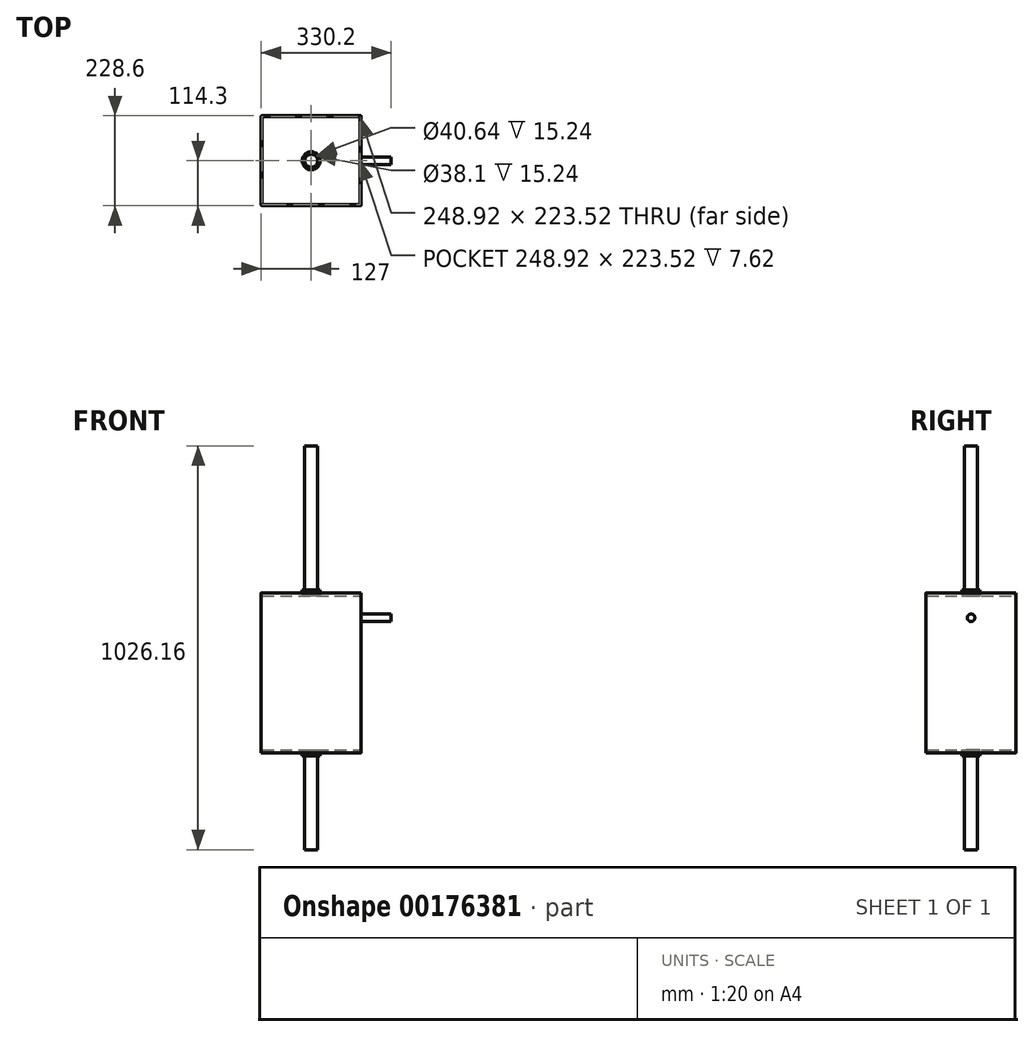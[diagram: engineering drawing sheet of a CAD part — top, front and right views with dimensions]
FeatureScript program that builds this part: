
annotation { "Feature Type Name" : "Feature", "Feature Type Description" : "" }
export const myFeature = defineFeature(function(context is Context, id is Id, definition is map)
    precondition{}
    {
        {
            var Q0;
            Q0=qCreatedBy(makeId("Front.planeOp"),FACE);
            var sketch = newSketch(context, id + "F0", { "sketchPlane" : qUnion([Q0])});
            skLineSegment(sketch, "E0.bottom", {"start": v(0, 406.4) * mm, "end": v(254, 406.4) * mm});
            skLineSegment(sketch, "E0.top", {"start": v(0, 0) * mm, "end": v(254, 0) * mm});
            skLineSegment(sketch, "E0.left", {"start": v(0, 406.4) * mm, "end": v(0, 0) * mm});
            skLineSegment(sketch, "E0.right", {"start": v(254, 406.4) * mm, "end": v(254, 0) * mm});
            skSolve(sketch);
        }
        {
            var Q0;
            Q0 = qSketchRegion(id + "F0", true);
            extrude(context, id + "F1", {"entities" : qUnion([Q0]), "depth" : 228.6 * mm});
        }
        {
            var Q0;
            Q0=makeQuery(id+"F1.opExtrude","SWEPT_FACE",FACE,{"disambiguationData":[OSD([sQuery(id+"F0.wireOp",EDGE,"E0.bottom")])]});
            var sketch = newSketch(context, id + "F2", { "sketchPlane" : qUnion([Q0])});
            skLineSegment(sketch, "E1.bottom", {"start": v(2.54, -226.06) * mm, "end": v(251.46, -226.06) * mm});
            skLineSegment(sketch, "E1.top", {"start": v(2.54, -2.54) * mm, "end": v(251.46, -2.54) * mm});
            skLineSegment(sketch, "E1.left", {"start": v(2.54, -226.06) * mm, "end": v(2.54, -2.54) * mm});
            skLineSegment(sketch, "E1.right", {"start": v(251.46, -226.06) * mm, "end": v(251.46, -2.54) * mm});
            skSolve(sketch);
        }
        {
            var Q0;
            Q0 = qSketchRegion(id + "F2", true);
            extrude(context, id + "F3", {"entities" : qUnion([Q0]), "operationType" : NewBodyOperationType.REMOVE, "oppositeDirection" : true, "depth" : 7.62 * mm});
        }
        {
            var Q0;
            Q0=makeQuery(id+"F1.opExtrude","SWEPT_FACE",FACE,{"disambiguationData":[OSD([sQuery(id+"F0.wireOp",EDGE,"E0.top")])]});
            var sketch = newSketch(context, id + "F4", { "sketchPlane" : qUnion([Q0])});
            skLineSegment(sketch, "E2.bottom", {"start": v(2.54, 226.06) * mm, "end": v(251.46, 226.06) * mm});
            skLineSegment(sketch, "E2.top", {"start": v(2.54, 2.54) * mm, "end": v(251.46, 2.54) * mm});
            skLineSegment(sketch, "E2.left", {"start": v(2.54, 226.06) * mm, "end": v(2.54, 2.54) * mm});
            skLineSegment(sketch, "E2.right", {"start": v(251.46, 226.06) * mm, "end": v(251.46, 2.54) * mm});
            skSolve(sketch);
        }
        {
            var Q0;
            Q0 = qSketchRegion(id + "F4", true);
            extrude(context, id + "F5", {"entities" : qUnion([Q0]), "operationType" : NewBodyOperationType.REMOVE, "oppositeDirection" : true, "depth" : 7.62 * mm});
        }
        {
            var Q0;
            Q0=makeQuery(id+"F5.boolean.opBoolean","COPY",FACE,{"derivedFrom":makeQuery(id+"F5.opExtrude","CAP_FACE",FACE,{"disambiguationData":[OSD([sQuery(id+"F4.wireOp",EDGE,"E2.bottom"),sQuery(id+"F4.wireOp",EDGE,"E2.top"),sQuery(id+"F4.wireOp",EDGE,"E2.left"),sQuery(id+"F4.wireOp",EDGE,"E2.right")])],"isStart":false})});
            var sketch = newSketch(context, id + "F6", { "sketchPlane" : qUnion([Q0])});
            skCircle(sketch, "E3", {"center": v(127, 114.3) * mm, "radius": 22.86 * mm});
            skCircle(sketch, "E4", {"center": v(127, 114.3) * mm, "radius": 20.32 * mm});
            skSolve(sketch);
        }
        {
            var Q0;
            Q0 = qSketchRegion(id + "F6", true);
            extrude(context, id + "F7", {"entities" : qUnion([Q0]), "depth" : 15.24 * mm});
        }
        {
            var Q0;
            Q0=makeQuery(id+"F5.boolean.opBoolean","COPY",FACE,{"derivedFrom":makeQuery(id+"F5.opExtrude","CAP_FACE",FACE,{"disambiguationData":[OSD([sQuery(id+"F4.wireOp",EDGE,"E2.bottom"),sQuery(id+"F4.wireOp",EDGE,"E2.top"),sQuery(id+"F4.wireOp",EDGE,"E2.left"),sQuery(id+"F4.wireOp",EDGE,"E2.right")])],"isStart":false})});
            var sketch = newSketch(context, id + "F8", { "sketchPlane" : qUnion([Q0])});
            skCircle(sketch, "E5", {"center": v(127, 114.3) * mm, "radius": 16.51 * mm});
            skSolve(sketch);
        }
        {
            var Q0;
            Q0 = qSketchRegion(id + "F8", true);
            var Q1;
            Q1 = qConstructionFilter(qBodyType(qCreatedBy(id + "F8" ,EDGE), BodyType.WIRE), ConstructionObject.NO);
            extrude(context, id + "F9", {"entities" : qUnion([Q0]), "surfaceEntities" : qUnion([Q1]), "depth" : 254 * mm});
        }
        {
            var Q0;
            Q0=makeQuery(id+"F1.opExtrude","CAP_EDGE",EDGE,{"disambiguationData":[OSD([sQuery(id+"F0.wireOp",EDGE,"E0.left")])],"isStart":false});
            var Q1;
            Q1=makeQuery(id+"F1.opExtrude","CAP_EDGE",EDGE,{"disambiguationData":[OSD([sQuery(id+"F0.wireOp",EDGE,"E0.left")])],"isStart":true});
            var Q2;
            {var subQ0=sQuery(id+"F0.wireOp",EDGE,"E0.bottom");var subQ1=sQuery(id+"F0.wireOp",EDGE,"E0.right");Q2=makeQuery(id+"FteSAe2NLqNJWqs_1.boolean.opBoolean","SPLIT",EDGE,{"disambiguationData":[TD([makeQuery(id+"F1.opExtrude","SWEPT_FACE",FACE,{"disambiguationData":[OSD([subQ0])]})])],"derivedFrom":makeQuery(id+"F1.opExtrude","CAP_EDGE",EDGE,{"disambiguationData":[OSD([subQ1])],"isStart":false})});}
            var Q3;
            {var subQ0=sQuery(id+"F0.wireOp",EDGE,"E0.bottom");var subQ1=sQuery(id+"F0.wireOp",EDGE,"E0.right");Q3=makeQuery(id+"FteSAe2NLqNJWqs_1.boolean.opBoolean","SPLIT",EDGE,{"disambiguationData":[TD([makeQuery(id+"F1.opExtrude","SWEPT_FACE",FACE,{"disambiguationData":[OSD([subQ0])]})])],"derivedFrom":makeQuery(id+"F1.opExtrude","CAP_EDGE",EDGE,{"disambiguationData":[OSD([subQ1])],"isStart":true})});}
            var Q4;
            {var subQ0=sQuery(id+"F0.wireOp",EDGE,"E0.right");var subQ1=sQuery(id+"F0.wireOp",EDGE,"E0.top");Q4=makeQuery(id+"FteSAe2NLqNJWqs_1.boolean.opBoolean","SPLIT",EDGE,{"disambiguationData":[TD([makeQuery(id+"F1.opExtrude","SWEPT_FACE",FACE,{"disambiguationData":[OSD([subQ1])]})])],"derivedFrom":makeQuery(id+"F1.opExtrude","CAP_EDGE",EDGE,{"disambiguationData":[OSD([subQ0])],"isStart":false})});}
            var Q5;
            {var subQ0=sQuery(id+"F0.wireOp",EDGE,"E0.right");var subQ1=sQuery(id+"F0.wireOp",EDGE,"E0.top");Q5=makeQuery(id+"FteSAe2NLqNJWqs_1.boolean.opBoolean","SPLIT",EDGE,{"disambiguationData":[TD([makeQuery(id+"F1.opExtrude","SWEPT_FACE",FACE,{"disambiguationData":[OSD([subQ1])]})])],"derivedFrom":makeQuery(id+"F1.opExtrude","CAP_EDGE",EDGE,{"disambiguationData":[OSD([subQ0])],"isStart":true})});}
            fillet(context, id + "F10", {"entities" : qUnion([Q0, Q1, Q2, Q3, Q4, Q5]), "radius" : 1.78 * mm, "tangentPropagation" : true, "allowEdgeOverflow" : false});
        }
        {
            var Q0;
            Q0=makeQuery(id+"F3.boolean.opBoolean","COPY",FACE,{"derivedFrom":makeQuery(id+"F3.opExtrude","CAP_FACE",FACE,{"disambiguationData":[OSD([sQuery(id+"F2.wireOp",EDGE,"E1.bottom"),sQuery(id+"F2.wireOp",EDGE,"E1.top"),sQuery(id+"F2.wireOp",EDGE,"E1.left"),sQuery(id+"F2.wireOp",EDGE,"E1.right")])],"isStart":false})});
            var sketch = newSketch(context, id + "F11", { "sketchPlane" : qUnion([Q0])});
            skCircle(sketch, "E6", {"center": v(127, -114.3) * mm, "radius": 22.86 * mm});
            skCircle(sketch, "E7", {"center": v(127, -114.3) * mm, "radius": 19.05 * mm});
            skSolve(sketch);
        }
        {
            var Q0;
            Q0 = qSketchRegion(id + "F11", true);
            extrude(context, id + "F12", {"entities" : qUnion([Q0]), "depth" : 15.24 * mm});
        }
        {
            var Q0;
            Q0=makeQuery(id+"F3.boolean.opBoolean","COPY",FACE,{"derivedFrom":makeQuery(id+"F3.opExtrude","CAP_FACE",FACE,{"disambiguationData":[OSD([sQuery(id+"F2.wireOp",EDGE,"E1.bottom"),sQuery(id+"F2.wireOp",EDGE,"E1.top"),sQuery(id+"F2.wireOp",EDGE,"E1.left"),sQuery(id+"F2.wireOp",EDGE,"E1.right")])],"isStart":false})});
            var sketch = newSketch(context, id + "F13", { "sketchPlane" : qUnion([Q0])});
            skCircle(sketch, "E8", {"center": v(127, -114.3) * mm, "radius": 16.51 * mm});
            skSolve(sketch);
        }
        {
            var Q0;
            Q0 = qSketchRegion(id + "F13", true);
            var Q1;
            Q1 = qConstructionFilter(qBodyType(qCreatedBy(id + "F13" ,EDGE), BodyType.WIRE), ConstructionObject.NO);
            extrude(context, id + "F14", {"entities" : qUnion([Q0]), "surfaceEntities" : qUnion([Q1]), "depth" : 381 * mm});
        }
        {
            var Q0;
            Q0=makeQuery(id+"F1.opExtrude","SWEPT_FACE",FACE,{"disambiguationData":[OSD([sQuery(id+"F0.wireOp",EDGE,"E0.right")])]});
            var sketch = newSketch(context, id + "F15", { "sketchPlane" : qUnion([Q0])});
            skCircle(sketch, "E9", {"center": v(-114.3, 342.9) * mm, "radius": 9.53 * mm});
            skSolve(sketch);
        }
        {
            var Q0;
            Q0 = qSketchRegion(id + "F15", true);
            extrude(context, id + "F16", {"entities" : qUnion([Q0]), "operationType" : NewBodyOperationType.ADD, "depth" : 76.2 * mm});
        }
    });
